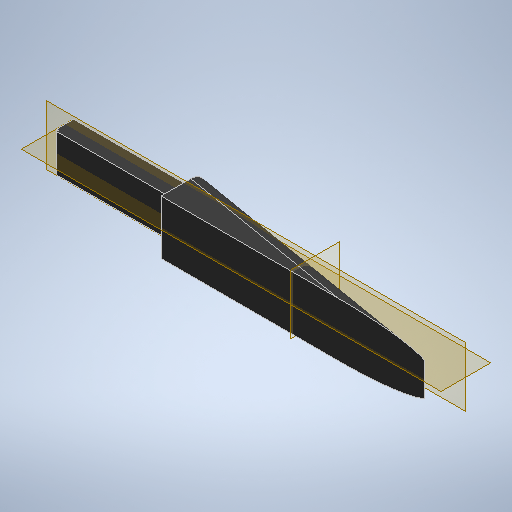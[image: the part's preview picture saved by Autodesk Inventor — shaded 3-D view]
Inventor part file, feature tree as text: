
AUTODESK INVENTOR PART (.ipt)
format: ipt  version: 2025.2 (Build 292293000, 293)  size: 288,768 bytes
history: native  units: mm
features: extrude x4, sketch x4, fillet x1
ambient origin geometry x8: Origin, YZ Plane, XZ Plane, XY Plane, X Axis, Y Axis, Z Axis, Center Point
bodies: Solid1 (feature_tree)
feature tree (9):
  extrude  "Extrusion1"  Depth=18.0mm
  extrude  "Extrusion2"  Depth=0.25mm
  extrude  "Extrusion4"  Depth=12.5mm
  extrude  "Extrusion5"  Depth=38.75mm TaperAngle=0.0deg
  fillet  "Fillet2"  Radius=5.0mm
  sketch  "Sketch1"  dims[d0=87.5mm d1=18.0mm]
  sketch  "Sketch3"  dims[d2=15.0mm d3=0.0mm d5=0.25mm]
  sketch  "Sketch5"  dims[d6=0.0mm d7=0.0mm d14=12.5mm]
  sketch  "Sketch7"  dims[d15=5.65mm d16=38.75mm d17=0.0mm d19=5.0mm d23=98.0mm d24=175.45mm d25=5.65mm d26=0.0mm d28=3.95mm d29=4.7mm]
